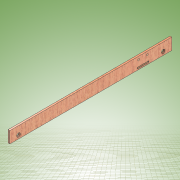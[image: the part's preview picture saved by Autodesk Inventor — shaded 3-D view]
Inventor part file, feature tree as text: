
AUTODESK INVENTOR PART (.ipt)
format: ipt  version: 2022 (Build 260153000, 153)  size: 153,088 bytes
history: native  units: mm
features: extrude x2, sketch x2, other x1
ambient origin geometry x8: Origin, YZ Plane, XZ Plane, XY Plane, X Axis, Y Axis, Z Axis, Center Point
bodies: Body1 (feature_tree)
feature tree (5):
  other  "Sólido1"
  extrude  "Extrusión1"  Depth=280.0mm
  extrude  "Extrusión2"  Depth=3.0mm TaperAngle=0.0deg
  sketch  "Boceto1"  dims[d0=20.0mm d1=280.0mm]
  sketch  "Boceto2"  dims[d2=6.35mm d6=3.0mm d7=0.0mm d8=6.0mm d9=250.0mm d10=15.0mm d11=20.0mm d12=15.0mm d13=40.0mm d14=2.0mm d15=3.0mm d16=2.54mm d17=2.54mm d18=0.0mm d19=0.0mm]
